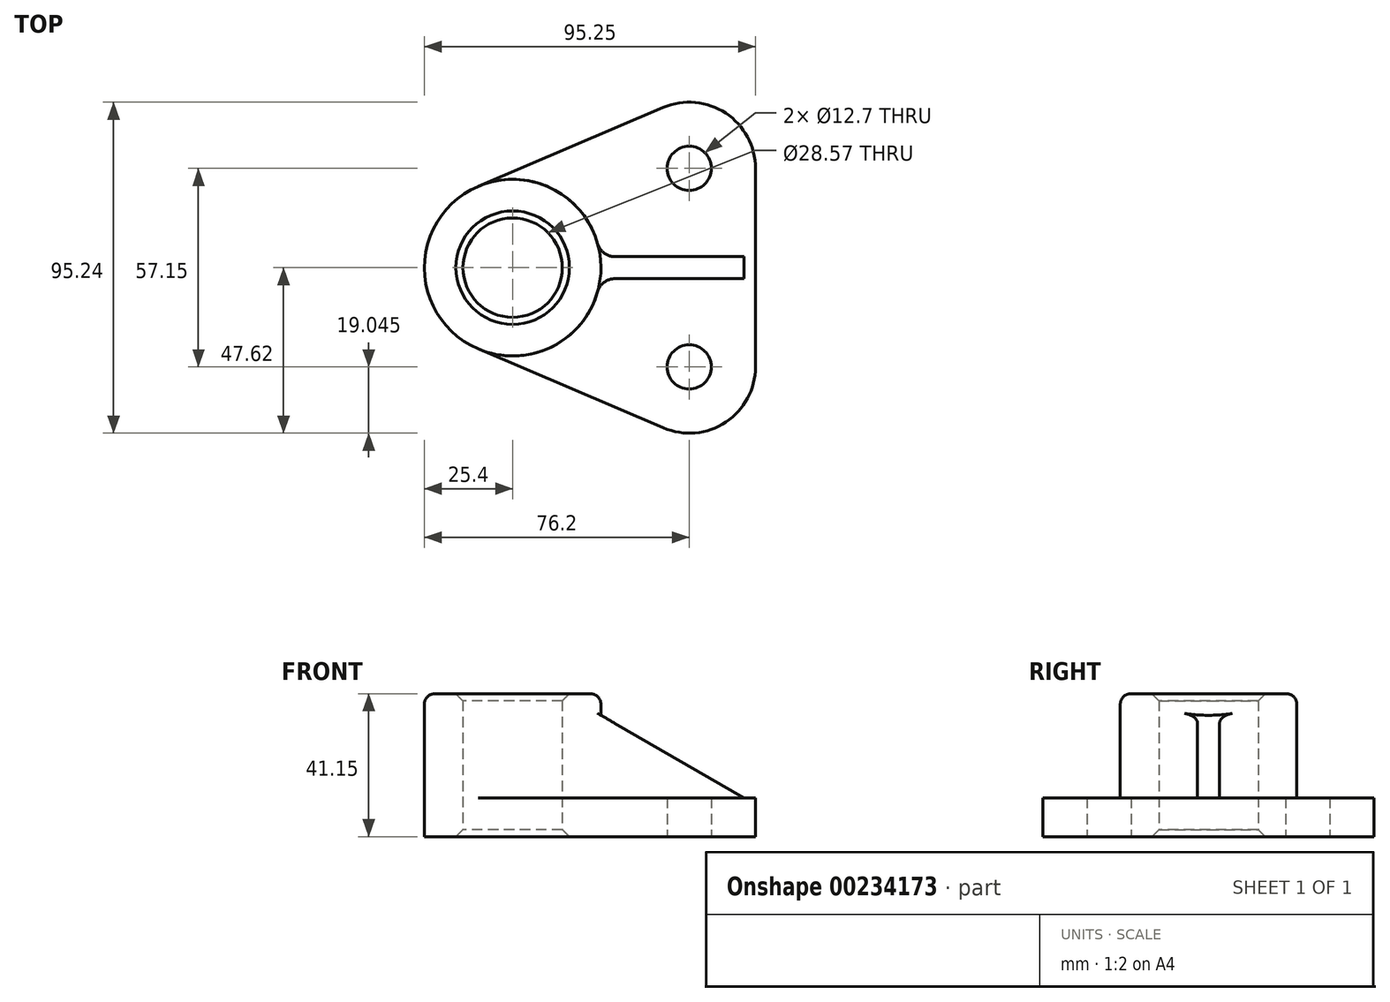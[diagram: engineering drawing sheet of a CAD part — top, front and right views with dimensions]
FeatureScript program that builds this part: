
annotation { "Feature Type Name" : "Feature", "Feature Type Description" : "" }
export const myFeature = defineFeature(function(context is Context, id is Id, definition is map)
    precondition{}
    {
        {
            var Q0;
            Q0=qCreatedBy(makeId("Top.planeOp"),FACE);
            var sketch = newSketch(context, id + "F0", { "sketchPlane" : qUnion([Q0])});
            skCircle(sketch, "E0", {"center": v(0, 0) * mm, "radius": 25.4 * mm});
            skCircle(sketch, "E1", {"center": v(0, 0) * mm, "radius": 14.29 * mm});
            skLineSegment(sketch, "E2", {"start": v(0, 0) * mm, "end": v(50.8, 0) * mm, "construction": true});
            skCircle(sketch, "E3", {"center": v(50.8, 28.58) * mm, "radius": 6.35 * mm});
            skArc(sketch, "E4", {"start": v(69.85, 28.58) * mm, "mid": v(61.3, 44.47) * mm, "end": v(43.33, 46.1) * mm});
            skLineSegment(sketch, "E5", {"start": v(-9.97, 23.36) * mm, "end": v(43.33, 46.1) * mm});
            skLineSegment(sketch, "E6", {"start": v(69.85, 28.58) * mm, "end": v(69.85, 0) * mm});
            skLineSegment(sketch, "E7", {"start": v(50.8, 0) * mm, "end": v(86.08, 0) * mm, "construction": true});
            skLineSegment(sketch, "E8.MirrorCS", {"start": v(-9.97, -23.36) * mm, "end": v(43.33, -46.1) * mm});
            skArc(sketch, "E9.MirrorCS", {"start": v(69.85, -28.58) * mm, "mid": v(61.3, -44.47) * mm, "end": v(43.33, -46.1) * mm});
            skLineSegment(sketch, "E10.MirrorCS", {"start": v(69.85, -28.58) * mm, "end": v(69.85, 0) * mm});
            skCircle(sketch, "E11.MirrorC", {"center": v(50.8, -28.58) * mm, "radius": 6.35 * mm});
            skSolve(sketch);
        }
        {
            var Q0;
            Q0=qSketchRegion(id+"F0",true);
            extrude(context, id + "F1", {"entities" : qUnion([Q0]), "depth" : 11.18 * mm});
        }
        {
            var Q0;
            Q0=makeQuery(id+"F1.opExtrude","CAP_FACE",FACE,{"disambiguationData":[OSD([sQuery(id+"F0.wireOp",EDGE,"E0"),sQuery(id+"F0.wireOp",EDGE,"E1"),sQuery(id+"F0.wireOp",EDGE,"E3"),sQuery(id+"F0.wireOp",EDGE,"E4"),sQuery(id+"F0.wireOp",EDGE,"E5"),sQuery(id+"F0.wireOp",EDGE,"E6"),sQuery(id+"F0.wireOp",EDGE,"E8.MirrorCS"),sQuery(id+"F0.wireOp",EDGE,"E9.MirrorCS"),sQuery(id+"F0.wireOp",EDGE,"E10.MirrorCS"),sQuery(id+"F0.wireOp",EDGE,"E11.MirrorC")])],"isStart":false});
            var sketch = newSketch(context, id + "F2", { "sketchPlane" : qUnion([Q0])});
            skCircle(sketch, "E12", {"center": v(0, 0) * mm, "radius": 25.4 * mm});
            skCircle(sketch, "E13", {"center": v(0, 0) * mm, "radius": 14.29 * mm});
            skSolve(sketch);
        }
        {
            var Q0;
            Q0=qSketchRegion(id+"F2",true);
            extrude(context, id + "F3", {"entities" : qUnion([Q0]), "operationType" : NewBodyOperationType.ADD, "depth" : 29.97 * mm});
        }
        {
            var Q0;
            Q0=qCreatedBy(makeId("Front.planeOp"),FACE);
            var sketch = newSketch(context, id + "F4", { "sketchPlane" : qUnion([Q0])});
            skLineSegment(sketch, "E14", {"start": v(18.45, 11.18) * mm, "end": v(66.55, 11.18) * mm});
            skLineSegment(sketch, "E15", {"start": v(66.55, 11.18) * mm, "end": v(18.45, 38.95) * mm});
            skLineSegment(sketch, "E16", {"start": v(18.45, 11.18) * mm, "end": v(18.45, 38.95) * mm});
            skSolve(sketch);
        }
        {
            var Q0;
            Q0=qSketchRegion(id+"F4",true);
            extrude(context, id + "F5", {"entities" : qUnion([Q0]), "operationType" : NewBodyOperationType.ADD, "endBound" : BoundingType.SYMMETRIC, "depth" : 6.38 * mm});
        }
        {
            var Q0;
            {var subQ0=sQuery(id+"F0.wireOp",EDGE,"E8.MirrorCS");var subQ2=sQuery(id+"F2.wireOp",EDGE,"E12");Q0=makeQuery(id+"F5.boolean.opBoolean","SPLIT",EDGE,{"disambiguationData":[TD([makeQuery(id+"F1.opExtrude","SWEPT_FACE",FACE,{"disambiguationData":[OSD([subQ0])]})])],"derivedFrom":makeQuery(id+"F3.opExtrude","CAP_EDGE",EDGE,{"disambiguationData":[OSD([subQ2])],"isStart":true})});}
            var Q1;
            Q1=makeQuery(id+"F5.opExtrude","CAP_EDGE",EDGE,{"disambiguationData":[OSD([sQuery(id+"F4.wireOp",EDGE,"E14")])],"isStart":false});
            var Q2;
            Q2=makeQuery(id+"F5.boolean.opBoolean","INTERSECT",EDGE,{"derivedFrom":[makeQuery(id+"F3.boolean.opBoolean","MERGE",FACE,{"derivedFrom":[makeQuery(id+"F1.opExtrude","SWEPT_FACE",FACE,{"disambiguationData":[OSD([sQuery(id+"F0.wireOp",EDGE,"E0")])]}),makeQuery(id+"F3.opExtrude","SWEPT_FACE",FACE,{"disambiguationData":[OSD([sQuery(id+"F2.wireOp",EDGE,"E12")])]})]}),makeQuery(id+"F5.opExtrude","CAP_FACE",FACE,{"disambiguationData":[OSD([sQuery(id+"F4.wireOp",EDGE,"E14"),sQuery(id+"F4.wireOp",EDGE,"E15"),sQuery(id+"F4.wireOp",EDGE,"E16")])],"isStart":false})]});
            var Q3;
            {var subQ0=sQuery(id+"F0.wireOp",EDGE,"E5");var subQ2=sQuery(id+"F2.wireOp",EDGE,"E12");Q3=makeQuery(id+"F5.boolean.opBoolean","SPLIT",EDGE,{"disambiguationData":[TD([makeQuery(id+"F1.opExtrude","SWEPT_FACE",FACE,{"disambiguationData":[OSD([subQ0])]})])],"derivedFrom":makeQuery(id+"F3.opExtrude","CAP_EDGE",EDGE,{"disambiguationData":[OSD([subQ2])],"isStart":true})});}
            var Q4;
            Q4=makeQuery(id+"F5.opExtrude","CAP_EDGE",EDGE,{"disambiguationData":[OSD([sQuery(id+"F4.wireOp",EDGE,"E14")])],"isStart":true});
            var Q5;
            Q5=makeQuery(id+"F5.boolean.opBoolean","INTERSECT",EDGE,{"derivedFrom":[makeQuery(id+"F3.boolean.opBoolean","MERGE",FACE,{"derivedFrom":[makeQuery(id+"F1.opExtrude","SWEPT_FACE",FACE,{"disambiguationData":[OSD([sQuery(id+"F0.wireOp",EDGE,"E0")])]}),makeQuery(id+"F3.opExtrude","SWEPT_FACE",FACE,{"disambiguationData":[OSD([sQuery(id+"F2.wireOp",EDGE,"E12")])]})]}),makeQuery(id+"F5.opExtrude","CAP_FACE",FACE,{"disambiguationData":[OSD([sQuery(id+"F4.wireOp",EDGE,"E14"),sQuery(id+"F4.wireOp",EDGE,"E15"),sQuery(id+"F4.wireOp",EDGE,"E16")])],"isStart":true})]});
            fillet(context, id + "F6", {"entities" : qUnion([Q0, Q1, Q2, Q3, Q4, Q5]), "radius" : 5.08 * mm, "tangentPropagation" : true, "allowEdgeOverflow" : false});
        }
        {
            var Q0;
            Q0=makeQuery(id+"F3.opExtrude","CAP_EDGE",EDGE,{"disambiguationData":[OSD([sQuery(id+"F2.wireOp",EDGE,"E12")])],"isStart":false});
            fillet(context, id + "F7", {"entities" : qUnion([Q0]), "radius" : 3.05 * mm, "tangentPropagation" : true, "allowEdgeOverflow" : false});
        }
        {
            var Q0;
            Q0=makeQuery(id+"F3.opExtrude","CAP_EDGE",EDGE,{"disambiguationData":[OSD([sQuery(id+"F2.wireOp",EDGE,"E13")])],"isStart":false});
            var Q1;
            Q1=makeQuery(id+"F1.opExtrude","CAP_EDGE",EDGE,{"disambiguationData":[OSD([sQuery(id+"F0.wireOp",EDGE,"E1")])],"isStart":true});
            chamfer(context, id + "F8", {"entities" : qUnion([Q0, Q1]), "chamferType" : ChamferType.OFFSET_ANGLE, "width" : 2.03 * mm, "oppositeDirection" : false, "angle" : 45 * degree, "tangentPropagation" : true});
        }
    });
